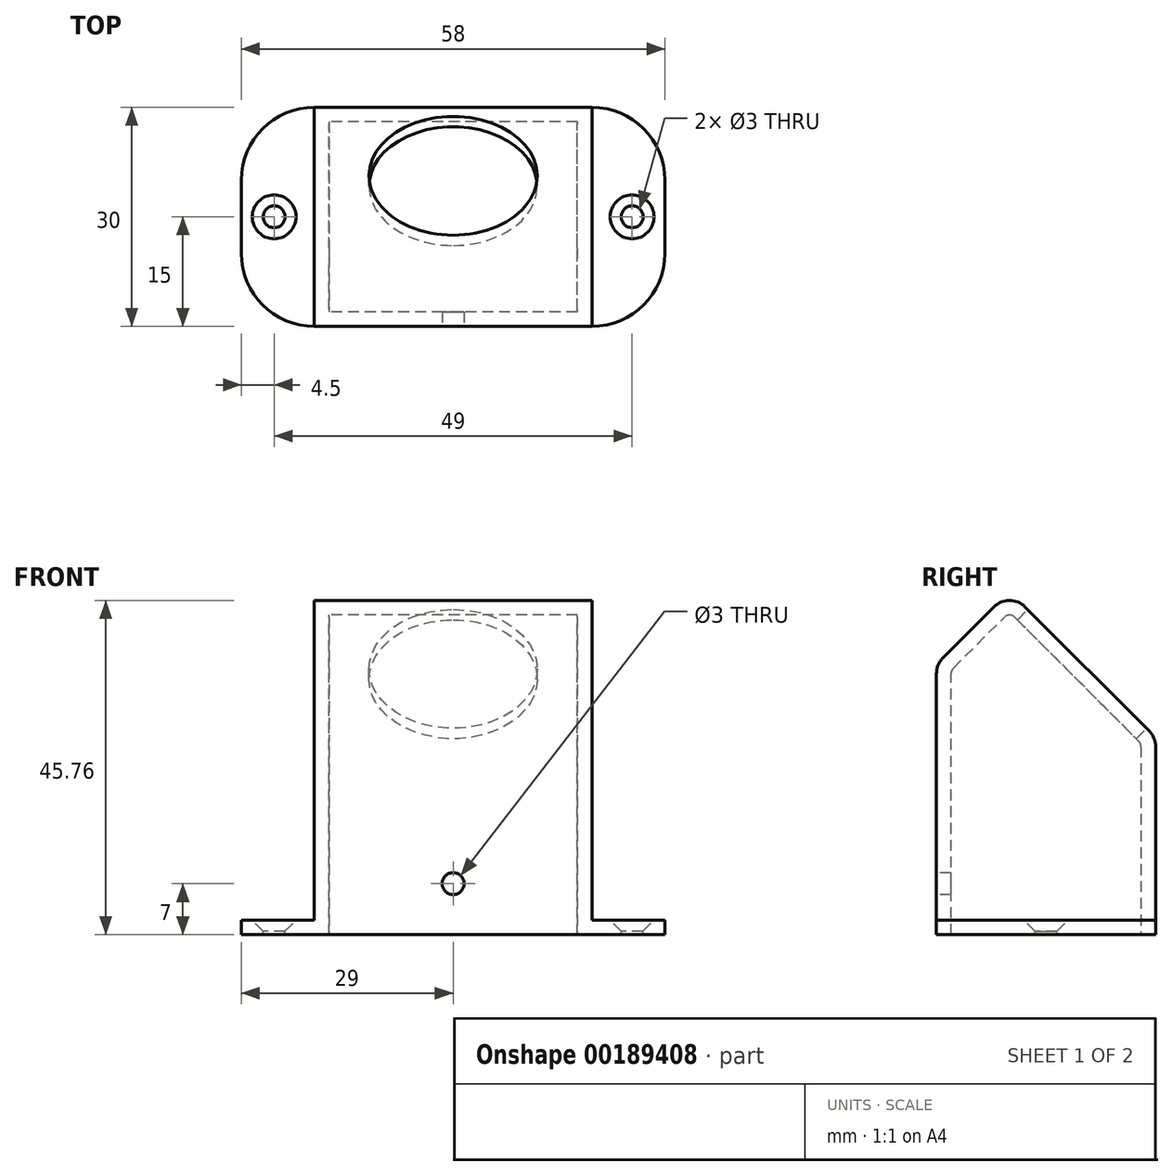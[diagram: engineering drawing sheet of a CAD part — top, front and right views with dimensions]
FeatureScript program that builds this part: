
annotation { "Feature Type Name" : "Feature", "Feature Type Description" : "" }
export const myFeature = defineFeature(function(context is Context, id is Id, definition is map)
    precondition{}
    {
        {
            var Q0;
            Q0=qCreatedBy(makeId("Right.planeOp"),FACE);
            var sketch = newSketch(context, id + "F0", { "sketchPlane" : qUnion([Q0])});
            skLineSegment(sketch, "E0.bottom", {"start": v(0, 0) * mm, "end": v(30, 0) * mm});
            skLineSegment(sketch, "E0.left", {"start": v(0, 0) * mm, "end": v(0, 35) * mm});
            skLineSegment(sketch, "E1", {"start": v(0, 35) * mm, "end": v(10, 45) * mm});
            skLineSegment(sketch, "E2", {"start": v(10, 45) * mm, "end": v(30, 25) * mm});
            skLineSegment(sketch, "E3", {"start": v(30, 25) * mm, "end": v(30, 0) * mm});
            skSolve(sketch);
        }
        {
            var Q0;
            Q0=makeQuery(id+"F0.imprint","IMPRINT",FACE,{"disambiguationData":[TD([[makeQuery(id+"F0.imprint","IMPRINT",EDGE,{"derivedFrom":sQuery(id+"F0.wireOp",EDGE,"E0.bottom")}),1.0]])]});
            extrude(context, id + "F1", {"entities" : qUnion([Q0]), "depth" : 19 * mm, "hasSecondDirection" : true, "secondDirectionOppositeDirection" : true, "secondDirectionDepth" : 19 * mm});
        }
        {
            var Q0;
            Q0=makeQuery(id+"F1.opExtrude","SWEPT_EDGE",EDGE,{"disambiguationData":[OSD([sQuery(id+"F0.wireOp",EDGE,"E1"),sQuery(id+"F0.wireOp",EDGE,"E2")])]});
            var Q1;
            Q1=makeQuery(id+"F1.opExtrude","SWEPT_EDGE",EDGE,{"disambiguationData":[OSD([sQuery(id+"F0.wireOp",EDGE,"E0.left"),sQuery(id+"F0.wireOp",EDGE,"E1")])]});
            var Q2;
            Q2=makeQuery(id+"F1.opExtrude","SWEPT_EDGE",EDGE,{"disambiguationData":[OSD([sQuery(id+"F0.wireOp",EDGE,"E2"),sQuery(id+"F0.wireOp",EDGE,"E3")])]});
            fillet(context, id + "F2", {"entities" : qUnion([Q0, Q1, Q2]), "radius" : 3 * mm, "tangentPropagation" : true, "allowEdgeOverflow" : false});
        }
        {
            var Q0;
            Q0=makeQuery(id+"F1.opExtrude","SWEPT_FACE",FACE,{"disambiguationData":[OSD([sQuery(id+"F0.wireOp",EDGE,"E0.bottom")])]});
            shell(context, id + "F3", {"entities" : qUnion([Q0]), "thickness" : 2 * mm});
        }
        {
            var Q0;
            Q0=qCreatedBy(makeId("Top.planeOp"),FACE);
            var sketch = newSketch(context, id + "F4", { "sketchPlane" : qUnion([Q0])});
            skLineSegment(sketch, "E4.bottom", {"start": v(29, 0) * mm, "end": v(-29, 0) * mm});
            skLineSegment(sketch, "E4.top", {"start": v(19, 30) * mm, "end": v(-29, 30) * mm});
            skLineSegment(sketch, "E4.left", {"start": v(29, 0) * mm, "end": v(29, 20) * mm});
            skLineSegment(sketch, "E4.right", {"start": v(-29, 0) * mm, "end": v(-29, 30) * mm});
            skLineSegment(sketch, "E5", {"start": v(0, 0) * mm, "end": v(0, 30) * mm, "construction": true});
            skLineSegment(sketch, "E6.0", {"start": v(17, 2) * mm, "end": v(17, 2) * mm});
            skLineSegment(sketch, "E6.1", {"start": v(-17, 38.5) * mm, "end": v(-17, 2) * mm});
            skLineSegment(sketch, "E6.2", {"start": v(-17, 2) * mm, "end": v(-17, 2) * mm});
            skLineSegment(sketch, "E6.3", {"start": v(17, 2) * mm, "end": v(-17, 2) * mm});
            skLineSegment(sketch, "E7.0", {"start": v(17, 2) * mm, "end": v(17, 28) * mm});
            skLineSegment(sketch, "E7.1", {"start": v(17, 28) * mm, "end": v(-17, 28) * mm});
            skPoint(sketch, "E8.visualSharp", {"position": v(29, 30) * mm});
            skArc(sketch, "E8.filletArc", {"start": v(29, 20) * mm, "mid": v(26.07, 27.07) * mm, "end": v(19, 30) * mm});
            skSolve(sketch);
        }
        {
            var Q0;
            Q0 = qSketchRegion(id + "F4", true);
            extrude(context, id + "F5", {"entities" : qUnion([Q0]), "operationType" : NewBodyOperationType.ADD, "oppositeDirection" : true, "depth" : 2 * mm});
        }
        {
            var Q0;
            Q0=makeQuery(id+"F1.opExtrude","SWEPT_FACE",FACE,{"disambiguationData":[OSD([sQuery(id+"F0.wireOp",EDGE,"E2")])]});
            var sketch = newSketch(context, id + "F6", { "sketchPlane" : qUnion([Q0])});
            skCircle(sketch, "E9", {"center": v(0, 9.73) * mm, "radius": 11.5 * mm});
            skPoint(sketch, "E9.centerSnap0", {"position": v(0, 9.73) * mm});
            skLineSegment(sketch, "E10", {"start": v(-19, 9.73) * mm, "end": v(19, 9.73) * mm, "construction": true});
            skSolve(sketch);
        }
        {
            var Q0;
            Q0 = qSketchRegion(id + "F6", true);
            extrude(context, id + "F7", {"entities" : qUnion([Q0]), "operationType" : NewBodyOperationType.REMOVE, "endBound" : BoundingType.UP_TO_NEXT, "oppositeDirection" : true, "depth" : 25 * mm});
        }
        {
            var Q0;
            {var subQ0=sQuery(id+"F4.wireOp",EDGE,"E4.bottom");var subQ3=sQuery(id+"F4.wireOp",EDGE,"E4.top");var subQ4=sQuery(id+"F4.wireOp",EDGE,"E4.left");Q0=makeQuery(id+"F5.boolean.opBoolean","SPLIT",FACE,{"disambiguationData":[TD([makeQuery(id+"F5.opExtrude","SWEPT_FACE",FACE,{"disambiguationData":[OSD([subQ4])]})])],"derivedFrom":makeQuery(id+"F5.opExtrude","CAP_FACE",FACE,{"disambiguationData":[OSD([subQ0,subQ3,subQ4,sQuery(id+"F4.wireOp",EDGE,"E4.right"),sQuery(id+"F4.wireOp",EDGE,"E6.0"),sQuery(id+"F4.wireOp",EDGE,"E6.1"),sQuery(id+"F4.wireOp",EDGE,"E6.2"),sQuery(id+"F4.wireOp",EDGE,"E6.3")])],"isStart":true})});}
            var sketch = newSketch(context, id + "F8", { "sketchPlane" : qUnion([Q0])});
            skLineSegment(sketch, "E11", {"start": v(32.2, 15) * mm, "end": v(-32.16, 15) * mm, "construction": true});
            skPoint(sketch, "E11.endSnap0", {"position": v(32.2, 15) * mm});
            skPoint(sketch, "E12", {"position": v(24.5, 15) * mm});
            skPoint(sketch, "E13", {"position": v(-24.5, 15) * mm});
            skSolve(sketch);
        }
        {
            var Q0;
            Q0=sQuery(id+"F8.wireOp",VERTEX,"E12");
            var Q1;
            Q1=sQuery(id+"F8.wireOp",VERTEX,"E13");
            var Q2;
            Q2=makeQuery(id+"F1.opExtrude","SWEPT_BODY",BODY,{"disambiguationData":[OSD([sQuery(id+"F0.wireOp",EDGE,"E0.bottom"),sQuery(id+"F0.wireOp",EDGE,"E0.left"),sQuery(id+"F0.wireOp",EDGE,"E0.right"),sQuery(id+"F0.wireOp",EDGE,"E1"),sQuery(id+"F0.wireOp",EDGE,"Cp6EldiS-K1VB-pbIQ-6EwE-Z1Az91EsJ0AK")])]});
            hole(context, id + "F9", {"style" : HoleStyle.C_SINK, "endStyle" : HoleEndStyle.THROUGH, "holeDiameter" : 3 * mm, "cSinkDiameter" : 6 * mm, "cSinkAngle" : 90 * degree, "startFromSketch" : true, "locations" : qUnion([Q0, Q1]), "scope" : qUnion([Q2]), "isTappedThrough" : true});
        }
        {
            var Q0;
            Q0=makeQuery(id+"F5.boolean.opBoolean","MERGE",FACE,{"derivedFrom":[makeQuery(id+"F1.opExtrude","SWEPT_FACE",FACE,{"disambiguationData":[OSD([sQuery(id+"F0.wireOp",EDGE,"E0.left")])]}),makeQuery(id+"F5.opExtrude","SWEPT_FACE",FACE,{"disambiguationData":[OSD([sQuery(id+"F4.wireOp",EDGE,"E4.bottom")])]})]});
            var sketch = newSketch(context, id + "F10", { "sketchPlane" : qUnion([Q0])});
            skPoint(sketch, "E14", {"position": v(0, 5) * mm});
            skSolve(sketch);
        }
        {
            var Q0;
            Q0=sQuery(id+"F10.wireOp",VERTEX,"E14");
            var Q1;
            Q1=makeQuery(id+"F1.opExtrude","SWEPT_BODY",BODY,{"disambiguationData":[OSD([sQuery(id+"F0.wireOp",EDGE,"E0.bottom"),sQuery(id+"F0.wireOp",EDGE,"E0.left"),sQuery(id+"F0.wireOp",EDGE,"E0.right"),sQuery(id+"F0.wireOp",EDGE,"E1"),sQuery(id+"F0.wireOp",EDGE,"Cp6EldiS-K1VB-pbIQ-6EwE-Z1Az91EsJ0AK")])]});
            hole(context, id + "F11", {"style" : HoleStyle.SIMPLE, "endStyle" : HoleEndStyle.BLIND, "holeDiameter" : 3 * mm, "holeDepth" : 12 * mm, "startFromSketch" : true, "locations" : qUnion([Q0]), "scope" : qUnion([Q1])});
        }
        {
            var Q0;
            Q0=makeQuery(id+"F5.opExtrude","SWEPT_EDGE",EDGE,{"disambiguationData":[OSD([sQuery(id+"F4.wireOp",EDGE,"E4.bottom"),sQuery(id+"F4.wireOp",EDGE,"E4.left")])]});
            fillet(context, id + "F12", {"entities" : qUnion([Q0]), "radius" : 10 * mm, "tangentPropagation" : true, "allowEdgeOverflow" : false});
        }
        {
            var Q0;
            Q0=makeQuery(id+"F5.opExtrude","SWEPT_EDGE",EDGE,{"disambiguationData":[OSD([sQuery(id+"F4.wireOp",EDGE,"E4.top"),sQuery(id+"F4.wireOp",EDGE,"E4.right")])]});
            fillet(context, id + "F13", {"entities" : qUnion([Q0]), "radius" : 10 * mm, "tangentPropagation" : true, "allowEdgeOverflow" : false});
        }
        {
            var Q0;
            Q0=makeQuery(id+"F5.opExtrude","SWEPT_EDGE",EDGE,{"disambiguationData":[OSD([sQuery(id+"F4.wireOp",EDGE,"E4.bottom"),sQuery(id+"F4.wireOp",EDGE,"E4.right")])]});
            fillet(context, id + "F14", {"entities" : qUnion([Q0]), "radius" : 10 * mm, "tangentPropagation" : true, "allowEdgeOverflow" : false});
        }
    });
